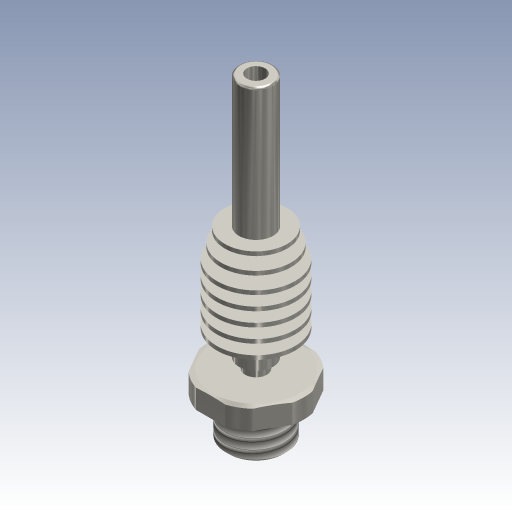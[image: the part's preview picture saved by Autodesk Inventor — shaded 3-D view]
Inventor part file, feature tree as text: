
AUTODESK INVENTOR PART (.ipt)
format: ipt  version: 2023.3 (Build 273359000, 359)  size: 360,960 bytes
history: native  units: mm (DEFAULTED — no unit token found)
features: other x8, extrude x2, sketch x1, thread x1, chamfer x1
ambient origin geometry x1: Ursprung
bodies: Volumenkörper1 (feature_tree)
feature tree (13):
  other  "heatbreak"
  sketch  "Skizze1"  dims[d0=3.0mm d1=6.0mm d2=10.0mm d3=0.0mm d4=10.0mm d5=0.0mm d6=6.0mm d7=0.0mm d8=0.3mm d9=2.0mm d10=45.0deg]
  extrude  "Extrusion1"  Depth=10.0mm
  extrude  "Extrusion2"  Depth=10.0mm TaperAngle=0.0deg
  thread  "Gewinde1"  [1 undecoded]
  chamfer  "Fase1"  Distance=6.0mm
  other  "YZ-Ebene"
  other  "XZ-Ebene"
  other  "XY-Ebene"
  other  "X-Achse"
  other  "Y-Achse"
  other  "Z-Achse"
  other  "Mittelpunkt"
note: 1 required parameter value undecoded (feature->parameter linkage not recoverable at this tier; creation-order binding heuristic only, values carry confidence <= 0.55)
